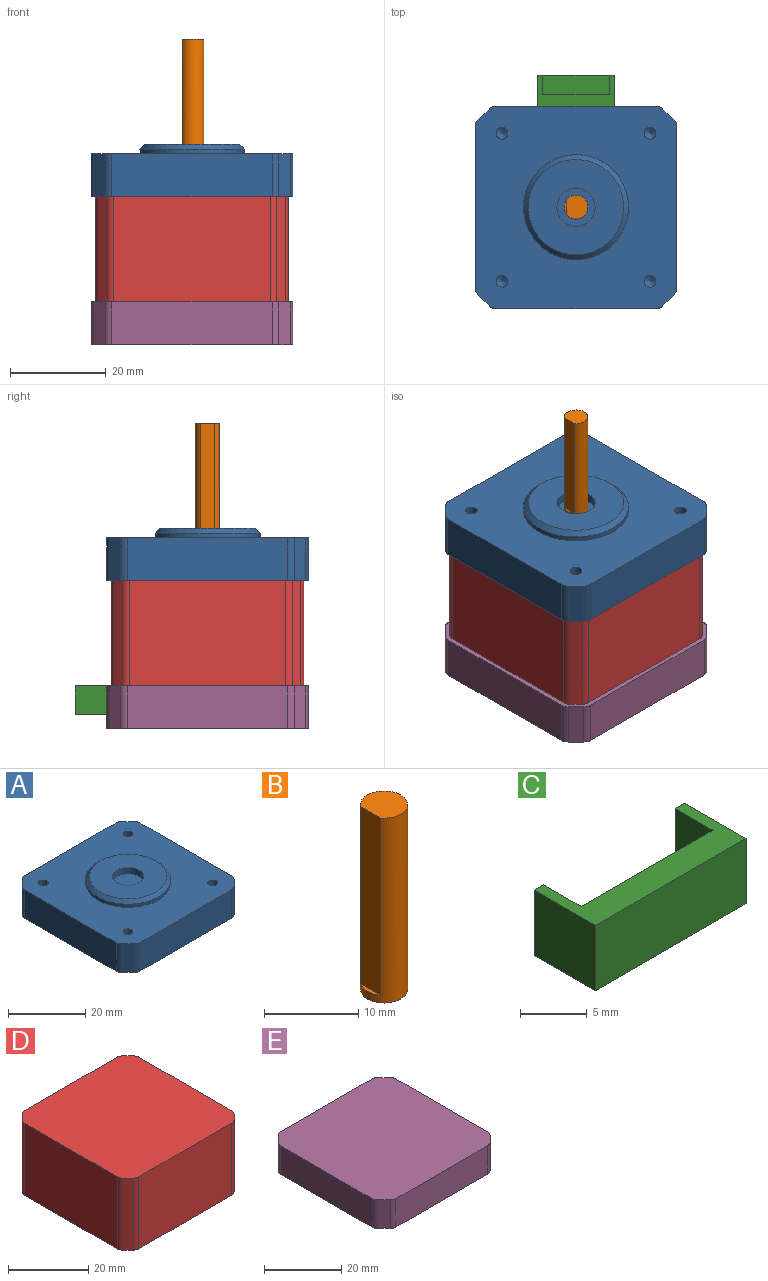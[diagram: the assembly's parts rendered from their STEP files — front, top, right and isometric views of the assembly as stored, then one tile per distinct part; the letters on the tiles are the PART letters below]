
ASSEMBLY  parts=5 mates=4
PART A: 31 faces, bbox 42.3x42.3x11 mm
  f0: plane 42.3x42.3mm, normal (0,0,-1), area 1763.6mm2, adj f1,f2,f3,f4,f6,f7,f8,f9
  f1: plane 33.57x9mm, normal (1,0,0), area 302.1mm2, adj f0,f5,f29,f30
  f2: plane 33.57x9mm, normal (0,1,0), area 302.1mm2, adj f0,f5,f23,f24
  f3: plane 33.57x9mm, normal (-1,0,0), area 302.1mm2, adj f0,f5,f25,f26
  f4: plane 33.57x9mm, normal (0,-1,0), area 302.1mm2, adj f0,f5,f27,f28
  f5: plane 42.3x42.3mm, normal (0,0,1), area 1363.8mm2, adj f1,f2,f3,f4,f6,f7,f8,f9
  f6: plane 9x2.36mm, normal (0.71,-0.71,0), area 30.1mm2, adj f0,f5,f27,f29
  f7: plane 9x2.36mm, normal (-0.71,-0.71,0), area 30.1mm2, adj f0,f5,f25,f28
  f8: plane 9x2.36mm, normal (0.71,0.71,0), area 30.1mm2, adj f0,f5,f23,f30
  f9: plane 9x2.36mm, normal (-0.71,0.71,0), area 30.1mm2, adj f0,f5,f24,f26
  f10: cylinder r=4mm len=8mm, axis (0,0,-1), area 50.3mm2, adj f12,f13
  f11: cylinder r=11mm len=22mm, axis (0,0,-1), area 69.1mm2, adj f5,f22
  f12: plane 20x20mm, normal (0,0,1), area 263.9mm2, adj f10,f22
  f13: plane 8x8mm, normal (0,0,1), area 50.3mm2, adj f10
  f14: cone r=0mm half-angle=59deg, axis (0,0,1), area 5.7mm2, adj f15
  f15: cylinder r=1.25mm len=3.5mm, axis (0,0,1), area 27.5mm2, adj f5,f14
  f16: cone r=0mm half-angle=59deg, axis (0,0,1), area 5.7mm2, adj f17
  f17: cylinder r=1.25mm len=3.5mm, axis (0,0,1), area 27.5mm2, adj f5,f16
  f18: cone r=0mm half-angle=59deg, axis (0,0,1), area 5.7mm2, adj f19
  f19: cylinder r=1.25mm len=3.5mm, axis (0,0,1), area 27.5mm2, adj f5,f18
  f20: cone r=0mm half-angle=59deg, axis (0,0,1), area 5.7mm2, adj f21
  f21: cylinder r=1.25mm len=3.5mm, axis (0,0,1), area 27.5mm2, adj f5,f20
  f22: cone r=10mm half-angle=45deg, axis (0,0,-1), area 93.3mm2, adj f11,f12
  f23: cylinder r=2mm len=9mm, axis (0,0,1), area 14.1mm2, adj f0,f2,f5,f8
  f24: cylinder r=2mm len=9mm, axis (0,0,1), area 14.1mm2, adj f0,f2,f5,f9
  f25: cylinder r=2mm len=9mm, axis (0,0,-1), area 14.1mm2, adj f0,f3,f5,f7
  f26: cylinder r=2mm len=9mm, axis (0,0,-1), area 14.1mm2, adj f0,f3,f5,f9
  f27: cylinder r=2mm len=9mm, axis (0,0,-1), area 14.1mm2, adj f0,f4,f5,f6
  f28: cylinder r=2mm len=9mm, axis (0,0,-1), area 14.1mm2, adj f0,f4,f5,f7
  f29: cylinder r=2mm len=9mm, axis (0,0,1), area 14.1mm2, adj f0,f1,f5,f6
  f30: cylinder r=2mm len=9mm, axis (0,0,1), area 14.1mm2, adj f0,f1,f5,f8
PART B: 5 faces, bbox 5x5x24 mm
  f0: cylinder r=2.5mm len=24mm, axis (0,0,-1), area 303mm2, adj f1,f2,f3,f4
  f1: plane 5x4.5mm, normal (0,0,1), area 18.6mm2, adj f0,f3
  f2: plane 5x5mm, normal (0,0,-1), area 19.6mm2, adj f0
  f3: plane 23x3mm, normal (-1,0,0), area 69mm2, adj f0,f1,f4
  f4: plane 3x0.5mm, normal (0,0,1), area 1mm2, adj f0,f3
PART C: 10 faces, bbox 16x6.5x6 mm
  f0: plane 16x6.5mm, normal (0,0,1), area 48mm2, adj f1,f3,f4,f5,f6,f8,f9
  f1: plane 6.5x6mm, normal (1,0,0), area 39mm2, adj f0,f2,f4,f5
  f2: plane 16x6.5mm, normal (0,0,-1), area 104mm2, adj f1,f3,f4,f5
  f3: plane 6.5x6mm, normal (-1,0,0), area 39mm2, adj f0,f2,f4,f5
  f4: plane 16x6mm, normal (0,1,0), area 26mm2, adj f0,f1,f2,f3,f6,f7,f8
  f5: plane 16x6mm, normal (0,-1,0), area 96mm2, adj f0,f1,f2,f3
  f6: plane 5x4mm, normal (-1,0,0), area 20mm2, adj f0,f4,f7,f9
  f7: plane 14x4mm, normal (0,0,1), area 56mm2, adj f4,f6,f8,f9
  f8: plane 5x4mm, normal (1,0,0), area 20mm2, adj f0,f4,f7,f9
  f9: plane 14x5mm, normal (0,1,0), area 70mm2, adj f0,f6,f7,f8
PART D: 18 faces, bbox 40.3x40.3x22 mm
  f0: plane 22x1.78mm, normal (-0.71,0.71,0), area 55.3mm2, adj f8,f9,f10,f17
  f1: plane 32.74x22mm, normal (-1,0,0), area 720.4mm2, adj f8,f9,f10,f11
  f2: plane 22x1.78mm, normal (-0.71,-0.71,0), area 55.3mm2, adj f8,f9,f11,f12
  f3: plane 32.74x22mm, normal (0,-1,0), area 720.4mm2, adj f8,f9,f12,f13
  f4: plane 22x1.78mm, normal (0.71,-0.71,0), area 55.3mm2, adj f8,f9,f13,f14
  f5: plane 32.74x22mm, normal (1,0,0), area 720.4mm2, adj f8,f9,f14,f15
  f6: plane 22x1.78mm, normal (0.71,0.71,0), area 55.3mm2, adj f8,f9,f15,f16
  f7: plane 32.74x22mm, normal (0,1,0), area 720.4mm2, adj f8,f9,f16,f17
  f8: plane 40.3x40.3mm, normal (0,0,1), area 1606mm2, adj f0,f1,f2,f3,f4,f5,f6,f7
  f9: plane 40.3x40.3mm, normal (0,0,-1), area 1606mm2, adj f0,f1,f2,f3,f4,f5,f6,f7
  f10: cylinder r=2mm len=22mm, axis (0,0,-1), area 34.6mm2, adj f0,f1,f8,f9
  f11: cylinder r=2mm len=22mm, axis (0,0,-1), area 34.6mm2, adj f1,f2,f8,f9
  f12: cylinder r=2mm len=22mm, axis (0,0,-1), area 34.6mm2, adj f2,f3,f8,f9
  f13: cylinder r=2mm len=22mm, axis (0,0,-1), area 34.6mm2, adj f3,f4,f8,f9
  f14: cylinder r=2mm len=22mm, axis (0,0,-1), area 34.6mm2, adj f4,f5,f8,f9
  f15: cylinder r=2mm len=22mm, axis (0,0,-1), area 34.6mm2, adj f5,f6,f8,f9
  f16: cylinder r=2mm len=22mm, axis (0,0,-1), area 34.6mm2, adj f6,f7,f8,f9
  f17: cylinder r=2mm len=22mm, axis (0,0,-1), area 34.6mm2, adj f0,f7,f8,f9
PART E: 20 faces, bbox 42.3x42.3x9 mm
  f0: plane 33.57x9mm, normal (1,0,0), area 302.1mm2, adj f4,f5,f16,f17
  f1: plane 33.57x9mm, normal (0,1,0), area 302.1mm2, adj f4,f5,f18,f19
  f2: plane 33.57x9mm, normal (-1,0,0), area 302.1mm2, adj f4,f5,f14,f15
  f3: plane 33.57x9mm, normal (0,-1,0), area 302.1mm2, adj f4,f5,f12,f13
  f4: plane 42.3x42.3mm, normal (0,0,1), area 1763.6mm2, adj f0,f1,f2,f3,f6,f7,f8,f9
  f5: plane 42.3x42.3mm, normal (0,0,-1), area 1650.5mm2, adj f0,f1,f2,f3,f6,f7,f8,f9
  f6: plane 9x2.36mm, normal (0.71,0.71,0), area 30.1mm2, adj f4,f5,f16,f18
  f7: plane 9x2.36mm, normal (-0.71,0.71,0), area 30.1mm2, adj f4,f5,f14,f19
  f8: plane 9x2.36mm, normal (-0.71,-0.71,0), area 30.1mm2, adj f4,f5,f12,f15
  f9: plane 9x2.36mm, normal (0.71,-0.71,0), area 30.1mm2, adj f4,f5,f13,f17
  f10: plane 10x10mm, normal (0,0,-1), area 78.5mm2, adj f11
  f11: cone r=5mm half-angle=45deg, axis (0,0,-1), area 48.9mm2, adj f5,f10
  f12: cylinder r=2mm len=9mm, axis (0,0,-1), area 14.1mm2, adj f3,f4,f5,f8
  f13: cylinder r=2mm len=9mm, axis (0,0,-1), area 14.1mm2, adj f3,f4,f5,f9
  f14: cylinder r=2mm len=9mm, axis (0,0,-1), area 14.1mm2, adj f2,f4,f5,f7
  f15: cylinder r=2mm len=9mm, axis (0,0,-1), area 14.1mm2, adj f2,f4,f5,f8
  f16: cylinder r=2mm len=9mm, axis (0,0,1), area 14.1mm2, adj f0,f4,f5,f6
  f17: cylinder r=2mm len=9mm, axis (0,0,1), area 14.1mm2, adj f0,f4,f5,f9
  f18: cylinder r=2mm len=9mm, axis (0,0,1), area 14.1mm2, adj f1,f4,f5,f6
  f19: cylinder r=2mm len=9mm, axis (0,0,1), area 14.1mm2, adj f1,f4,f5,f7
PLACE A t=(-42.48,-9.94,-5.25)mm
PLACE B t=(-42.48,-9.94,-5.25)mm
PLACE C t=(-42.48,-9.94,-5.25)mm
PLACE D t=(-42.48,-9.94,-5.25)mm
PLACE E t=(-42.48,-9.94,-5.25)mm fixed
MATE fastened E.f11 <-> D.f9  axis (0,0,1) through (-42.48,-9.94,3.75)mm
MATE fastened D.f8 <-> A.f10  axis (0,0,1) through (-42.48,-9.94,25.75)mm
MATE fastened C.f5 <-> E.f1  axis (0,-1,0) through (-42.48,11.21,3.75)mm
MATE fastened A.f10 <-> B.f0  axis (0,0,1) through (-42.48,-9.94,34.75)mm
